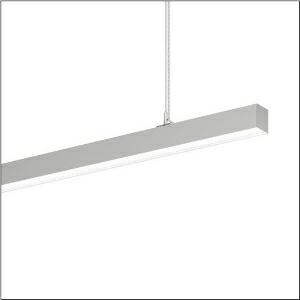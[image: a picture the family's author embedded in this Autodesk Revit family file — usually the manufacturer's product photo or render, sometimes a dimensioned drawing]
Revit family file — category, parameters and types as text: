
# Revit family: silica_r__21_51mx30tct9s_9c67
name_source: partatom
category: Lighting Fixtures
units: mm (PartAtom-declared; Revit-internal decimal feet)

## family parameters
Cut with Voids When Loaded = No
Host = Face
Light Source = No
Part Type = Normal
Room Calculation Point = No
Round Connector Dimension = Use Diameter
Shared = No

## types (1)
- --- (1 x LED, 10300 lm, 84.4 W, 6500K)
    Apparent Load = 84 VA
    CIE Flux Codes = 47 79 96 58 100
    Color Rendering = 80
    Color Temperature = 6500K
    Default Elevation = 1800 mm
    Description = Silica® 21, office luminaire, primary optical cover: cover, of PMMA, opal, light emission: direct/indirect distribution, primary light characteristic: symmetric, installation type: suspended mounting, LED, rated luminous flux: 10.300lm, luminous efficacy: 116lm/W, light colour: 8tw, colour temperature: 2700..6500K, control gear: DALI DT8, with terminal, 3+2-pole, max. 2.5mm², mains connection: 220..240V, AC, 50/60Hz, rated input power: 88.7W, luminaire housing, of aluminium, metallic grey (RAL 9006), length: 3.004mm, width: 53mm, height: 53mm, protection rating (complete): IP20, insulation class (complete): insulation class I (protective earthing), certification: CE, permissible operating ambient temperature: 0..+35°C, standard: EN 50419, packaging unit: 1 piece
    Height = 53 mm
    Lamp = 1 x LED
    Lamp Light Flux = 10300 lm
    Lamp Power = 84.4 W
    Lamp count = 1
    Length = 3004 mm
    Luminous efficacy = 122 lm/W
    Manufacturer = Siteco
    ModVariant = No
    Model = 51MX30TCT9S
    Mounting Place = Ceiling
    Mounting Type = Pendant
    Number of Poles = 1
    OnlyDefault = Yes
    Power Factor = 1
    Product Name = Silica® 21
    Product group = office luminaire | ceiling pendant
    ProductGroupID = 904
    Protection Class = Protection class I
    Protection Degree = IP 20
    RLX_Detail_Level = 1
    RLX_Emergency_Light_Flux = 0 lm
    RLX_Emergency_Type = 0
    RLX_Emergency_Type_DB = No
    RlxData = <blob elided: 20005 chars, md5=98dd5a42>
    Socket = socket
    Standby Power = 0 W
    System Light Flux = 10300 lm
    System Power = 84 W
    Type Comments = individual setting
    Type Image = l_1335864.jpg
    URL = http://relux.com
    VarID = @adj_139608
    Voltage = 0 V
    Weight = 0.00 kg
    Width = 53 mm

## geometry (parser evidence)
native form markers: Blend x4, Sweep x12
no freeform markers — native parametric forms only
